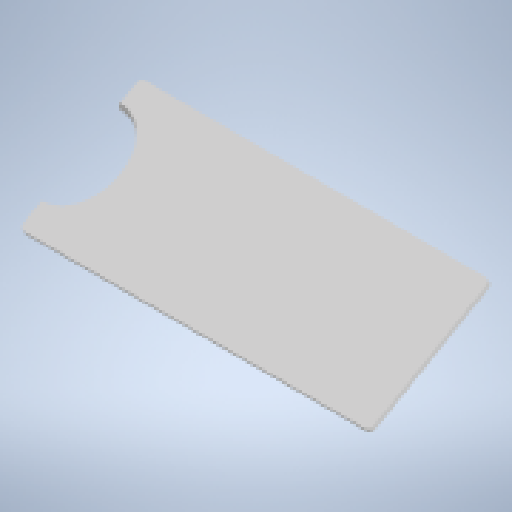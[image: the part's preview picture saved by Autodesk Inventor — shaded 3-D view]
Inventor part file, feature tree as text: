
AUTODESK INVENTOR PART (.ipt)
format: ipt  version: 2023.2 (Build 272271030, 271C)  size: 169,472 bytes
history: native  units: mm
features: extrude x2, sketch x2, fillet x1, other x1
ambient origin geometry x8: Origin, YZ Plane, XZ Plane, XY Plane, X Axis, Y Axis, Z Axis, Center Point
bodies: Solid1 (feature_tree)
feature tree (6):
  extrude  "Extrusion1"  TaperAngle=60.0deg  [1 undecoded]
  extrude  "Extrusion2"  Depth=150.0mm TaperAngle=0.0deg
  fillet  "Fillet1"  Radius=33.5mm
  sketch  "Sketch1"  dims[d0=60.0mm d1=60.0deg]
  sketch  "Sketch2"  dims[d2=2.0mm d3=150.0mm d4=0.0mm d5=33.5mm d6=0.0mm d7=0.0mm d8=2.0mm]
  other  "Definition1"
note: 1 required parameter value undecoded (feature->parameter linkage not recoverable at this tier; creation-order binding heuristic only, values carry confidence <= 0.55)
